# Revit family: Desk_Screens-Teknion-CQCSC_Smooth_Felt_Study_Carrel-R2019
name_source: partatom
category: Furniture
units: mm (PartAtom-declared; Revit-internal decimal feet)

## family parameters
Always vertical = Yes
Cut with Voids When Loaded = No
OmniClass Number = 23.40.20.00
OmniClass Title = General Furniture and Specialties
Room Calculation Point = No
Shared = Yes
Work Plane-Based = No

## types (6) — shared parameters
Assembly Code = E2020200
Manufacturer = Teknion
Manufacturer Fax = 416.661.4586
Part Number = CQCSC
Product Documentation Link = https://assets.teknion.com
Product Line = Routes
Product Page URL = https://www.teknion.com
Series = Routes
Sustainability Data = https://www.teknion.com
URL = www.teknion.com
Unit Weight URL = http://www.teknion.com
Warranty = http://www.teknion.com

## per-type parameters (varying)
| type | Actual Width | Description | Height | Model | Modesty Base Height | Width |
| 42" Datum Height, 24" Slim Modesty Base Height, 60" Width, 20" Depth | 62 " | Smooth Felt Study Carrel, 42" Datum Height, 24" Slim Modesty Base Height, 60" Width, 20" Depth | 42 " | CQCSC42L6020 | 24 " | 60 " |
| 42" Datum Height, 19" Semi Modesty Base Height, 60" Width, 20" Depth | 62 " | Smooth Felt Study Carrel, 42" Datum Height, 19" Semi Modesty Base Height, 60" Width, 20" Depth | 42 " | CQCSC42T6020 | 19 " | 60 " |
| 47" Datum Height, 24" Slim Modesty Base Height, 60" Width, 20" Depth | 62 " | Smooth Felt Study Carrel, 47" Datum Height, 24" Slim Modesty Base Height, 60" Width, 20" Depth | 47 " | CQCSC47L6020 | 24 " | 60 " |
| 42" Datum Height, 19" Semi Modesty Base Height, 72" Width, 20" Depth | 74 " | Smooth Felt Study Carrel, 42" Datum Height, 19" Semi Modesty Base Height, 72" Width, 20" Depth | 42 " | CQCSC42T7220 | 19 " | 72 " |
| 42" Datum Height, 24" Slim Modesty Base Height, 72" Width, 20" Depth | 74 " | Smooth Felt Study Carrel, 42" Datum Height, 24" Slim Modesty Base Height, 72" Width, 20" Depth | 42 " | CQCSC42L7220 | 24 " | 72 " |
| 47" Datum Height, 24" Slim Modesty Base Height, 72" Width, 20" Depth | 74 " | Smooth Felt Study Carrel, 47" Datum Height, 24" Slim Modesty Base Height, 72" Width, 20" Depth | 47 " | CQCSC47L7220 | 24 " | 72 " |

## geometry (parser evidence)
native form markers: Sweep x4
no freeform markers — native parametric forms only
